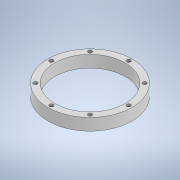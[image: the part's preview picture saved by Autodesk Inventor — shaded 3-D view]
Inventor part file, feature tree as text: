
AUTODESK INVENTOR PART (.ipt)
format: ipt  version: 2021 (Build 250183000, 183)  size: 132,608 bytes
history: native  units: mm
features: sketch x2, revolve x1, hole x1
ambient origin geometry x8: Origin, YZ Plane, XZ Plane, XY Plane, X Axis, Y Axis, Z Axis, Center Point
bodies: Solid1 (feature_tree)
feature tree (4):
  revolve  "Revolution1"  [1 undecoded]
  hole  "Hole1"  [1 undecoded]
  sketch  "Sketch1"  dims[d0=45.5mm d1=4.0mm]
  sketch  "Sketch2"  dims[d2=14.0mm d3=90.0deg d4=4.0mm d5=4.0mm d6=80.0mm d8=360.0deg d10=4.5mm d11=8.0mm d12=9.4mm d13=2.0mm d14=90.0deg d15=11.8mm d16=20.594885mm]
note: 2 required parameter values undecoded (feature->parameter linkage not recoverable at this tier; creation-order binding heuristic only, values carry confidence <= 0.55)